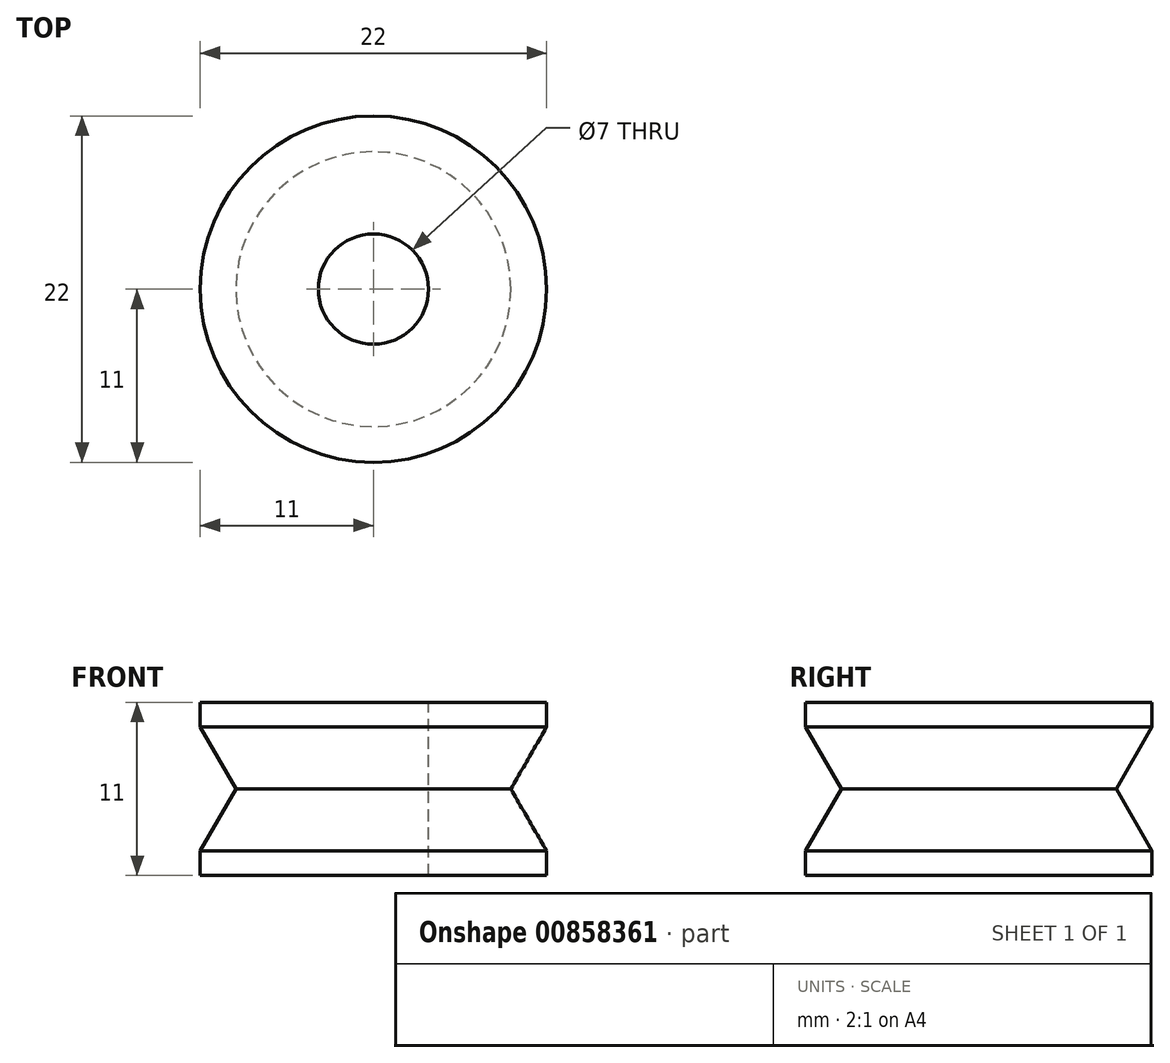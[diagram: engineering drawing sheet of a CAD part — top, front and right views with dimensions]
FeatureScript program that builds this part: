
annotation { "Feature Type Name" : "Feature", "Feature Type Description" : "" }
export const myFeature = defineFeature(function(context is Context, id is Id, definition is map)
    precondition{}
    {
        {
            var Q0;
            Q0=qCreatedBy(makeId("Front.planeOp"),FACE);
            var sketch = newSketch(context, id + "F0", { "sketchPlane" : qUnion([Q0])});
            skLineSegment(sketch, "E0", {"start": v(-3.5, -5.5) * mm, "end": v(-3.5, 5.5) * mm});
            skLineSegment(sketch, "E1", {"start": v(-3.5, 5.5) * mm, "end": v(-11, 5.5) * mm});
            skLineSegment(sketch, "E2", {"start": v(-11, 5.5) * mm, "end": v(-11, 3.94) * mm});
            skLineSegment(sketch, "E3", {"start": v(-11, 3.94) * mm, "end": v(-8.73, 0) * mm});
            skLineSegment(sketch, "E4", {"start": v(-8.73, 0) * mm, "end": v(-11, -3.94) * mm});
            skLineSegment(sketch, "E5", {"start": v(-11, -3.94) * mm, "end": v(-11, -5.5) * mm});
            skLineSegment(sketch, "E6", {"start": v(-11, -5.5) * mm, "end": v(-3.5, -5.5) * mm});
            skCircle(sketch, "E7", {"center": v(-14.5, 0) * mm, "radius": 5 * mm, "construction": true});
            skLineSegment(sketch, "E8", {"start": v(0, 0) * mm, "end": v(0, -16.78) * mm, "construction": true});
            skSolve(sketch);
        }
        {
            var Q0;
            Q0=makeQuery(id+"F0.imprint","IMPRINT",FACE,{"disambiguationData":[TD([[makeQuery(id+"F0.imprint","IMPRINT",EDGE,{"derivedFrom":sQuery(id+"F0.wireOp",EDGE,"E0")}),1.0]])]});
            var Q1;
            Q1=sQuery(id+"F0.wireOp",EDGE,"E8");
            var Q2;
            Q2=sQuery(id+"F0.wireOp",EDGE,"E8");
            revolve(context, id + "F1", {"surfaceOperationType" : NewSurfaceOperationType.NEW, "entities" : qUnion([Q0]), "surfaceEntities" : qUnion([Q1]), "axis" : qUnion([Q2]), "revolveType" : RevolveType.FULL});
        }
    });
